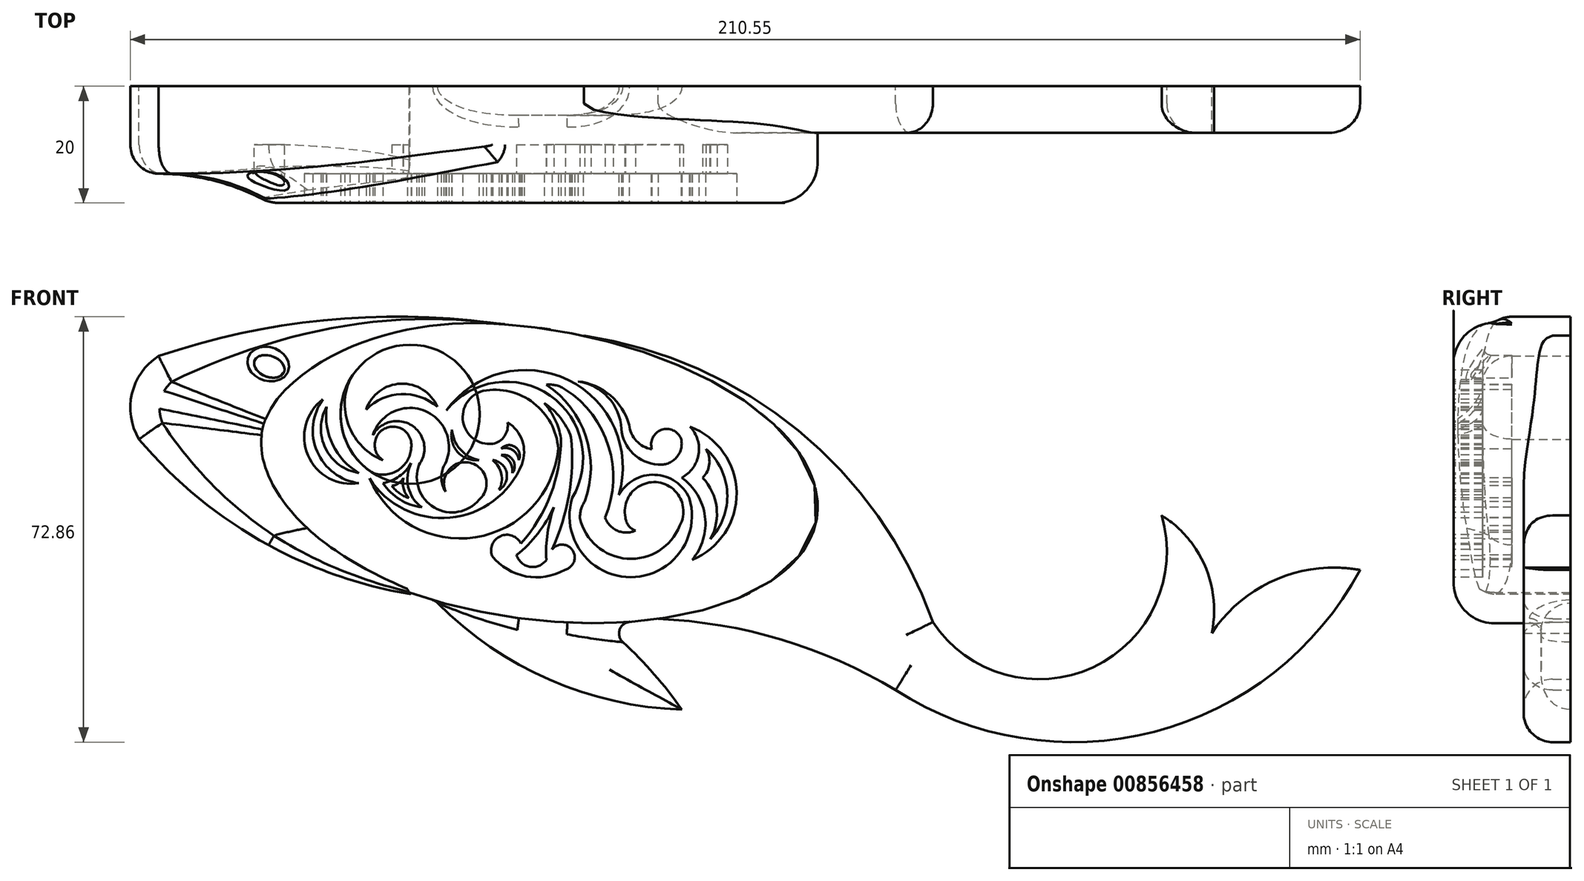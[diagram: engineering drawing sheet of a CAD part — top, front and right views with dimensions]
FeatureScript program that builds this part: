
annotation { "Feature Type Name" : "Feature", "Feature Type Description" : "" }
export const myFeature = defineFeature(function(context is Context, id is Id, definition is map)
    precondition{}
    {
        {
            var Q0;
            Q0=qCreatedBy(makeId("Front.planeOp"),FACE);
            var sketch = newSketch(context, id + "F0", { "sketchPlane" : qUnion([Q0])});
            skEllipse(sketch, "E0", {"center": v(0, 0) * mm, "majorRadius": 50 * mm, "minorRadius": 24.86 * mm, "majorAxis": v(-0.99, 0.15)});
            skArc(sketch, "E1", {"start": v(69.27, -25.55) * mm, "mid": v(46.22, 7.3) * mm, "end": v(9.53, 23.5) * mm});
            skArc(sketch, "E2", {"start": v(62.9, -37.19) * mm, "mid": v(43.33, -28.54) * mm, "end": v(22.22, -25) * mm});
            skArc(sketch, "E3", {"start": v(69.27, -25.55) * mm, "mid": v(96.72, -33.27) * mm, "end": v(108.45, -7.28) * mm});
            skArc(sketch, "E4", {"start": v(62.9, -37.19) * mm, "mid": v(107.17, -44.32) * mm, "end": v(142.42, -16.61) * mm});
            skArc(sketch, "E5", {"start": v(117.03, -27.44) * mm, "mid": v(115.9, -16) * mm, "end": v(108.45, -7.28) * mm});
            skArc(sketch, "E6", {"start": v(142.42, -16.61) * mm, "mid": v(128.1, -18.22) * mm, "end": v(117.03, -27.44) * mm});
            skArc(sketch, "E7", {"start": v(-20.37, -20.5) * mm, "mid": v(-4.53, -37.89) * mm, "end": v(17.35, -46.5) * mm});
            skArc(sketch, "E8", {"start": v(17.35, -46.5) * mm, "mid": v(9.14, -35.42) * mm, "end": v(0, -25.08) * mm});
            skArc(sketch, "E9", {"start": v(-5.05, 25.54) * mm, "mid": v(-34.49, 26.2) * mm, "end": v(-63.28, 20.02) * mm});
            skArc(sketch, "E10", {"start": v(-63.28, 20.02) * mm, "mid": v(-67.85, 13.59) * mm, "end": v(-66.64, 5.79) * mm});
            skArc(sketch, "E11", {"start": v(-66.64, 5.79) * mm, "mid": v(-45.3, -11.9) * mm, "end": v(-19.08, -20.93) * mm});
            skSolve(sketch);
        }
        {
            var Q0;
            {var subQ0=sQuery(id+"F0.wireOp",EDGE,"E0");var subQ5=makeQuery(id+"F0.imprint","INTERSECT",VERTEX,{"derivedFrom":[subQ0,sQuery(id+"F0.wireOp",EDGE,"E7")]});Q0=makeQuery(id+"F0.imprint","IMPRINT",FACE,{"disambiguationData":[TD([[makeQuery(id+"F0.imprint","IMPRINT",EDGE,{"disambiguationData":[TD([[subQ5,-1.0]])],"derivedFrom":subQ0}),1.0]])]});}
            extrude(context, id + "F1", {"entities" : qUnion([Q0]), "depth" : 20 * mm, "offsetDistance" : 25 * mm});
        }
        {
            var Q0;
            {var subQ4=sQuery(id+"F0.wireOp",EDGE,"E9");Q0=makeQuery(id+"F0.imprint","IMPRINT",FACE,{"disambiguationData":[TD([[makeQuery(id+"F0.imprint","IMPRINT",EDGE,{"derivedFrom":subQ4}),1.0]])]});}
            extrude(context, id + "F2", {"entities" : qUnion([Q0]), "operationType" : NewBodyOperationType.ADD, "depth" : 15 * mm, "offsetDistance" : 25 * mm});
        }
        {
            var Q0;
            {var subQ1=sQuery(id+"F0.wireOp",EDGE,"E1");Q0=makeQuery(id+"F0.imprint","IMPRINT",FACE,{"disambiguationData":[TD([[makeQuery(id+"F0.imprint","IMPRINT",EDGE,{"derivedFrom":subQ1}),1.0]])]});}
            extrude(context, id + "F3", {"entities" : qUnion([Q0]), "operationType" : NewBodyOperationType.ADD, "depth" : 8 * mm, "offsetDistance" : 25 * mm});
        }
        {
            var Q0;
            Q0=makeQuery(id+"F1.opExtrude","CAP_EDGE",EDGE,{"disambiguationData":[OSD([sQuery(id+"F0.wireOp",EDGE,"E0")])],"isStart":false});
            fillet(context, id + "F4", {"entities" : qUnion([Q0]), "radius" : 7 * mm, "tangentPropagation" : true, "allowEdgeOverflow" : false});
        }
        {
            var Q0;
            Q0=makeQuery(id+"F2.opExtrude","CAP_EDGE",EDGE,{"disambiguationData":[OSD([sQuery(id+"F0.wireOp",EDGE,"E11")])],"isStart":false});
            var Q1;
            Q1=makeQuery(id+"F2.opExtrude","CAP_EDGE",EDGE,{"disambiguationData":[OSD([sQuery(id+"F0.wireOp",EDGE,"E10")])],"isStart":false});
            var Q2;
            Q2=makeQuery(id+"F2.opExtrude","CAP_EDGE",EDGE,{"disambiguationData":[OSD([sQuery(id+"F0.wireOp",EDGE,"E9")])],"isStart":false});
            fillet(context, id + "F5", {"entities" : qUnion([Q0, Q1, Q2]), "radius" : 5 * mm, "tangentPropagation" : true, "allowEdgeOverflow" : false});
        }
        {
            var Q0;
            Q0=makeQuery(id+"F3.opExtrude","CAP_EDGE",EDGE,{"disambiguationData":[OSD([sQuery(id+"F0.wireOp",EDGE,"E2")])],"isStart":false});
            var Q1;
            Q1=makeQuery(id+"F3.opExtrude","CAP_EDGE",EDGE,{"disambiguationData":[OSD([sQuery(id+"F0.wireOp",EDGE,"E4")])],"isStart":false});
            var Q2;
            Q2=makeQuery(id+"F3.opExtrude","CAP_EDGE",EDGE,{"disambiguationData":[OSD([sQuery(id+"F0.wireOp",EDGE,"E3")])],"isStart":false});
            var Q3;
            Q3=makeQuery(id+"F3.opExtrude","CAP_EDGE",EDGE,{"disambiguationData":[OSD([sQuery(id+"F0.wireOp",EDGE,"E1")])],"isStart":false});
            fillet(context, id + "F6", {"entities" : qUnion([Q0, Q1, Q2, Q3]), "radius" : 5 * mm, "tangentPropagation" : true, "allowEdgeOverflow" : false});
        }
        {
            var Q0;
            {var subQ0=sQuery(id+"F0.wireOp",EDGE,"E0");Q0=makeQuery(id+"F4.opFillet","BLEND_EDGE",EDGE,{"blendedFrom":[makeQuery(id+"F1.opExtrude","CAP_EDGE",EDGE,{"disambiguationData":[OSD([subQ0])],"isStart":false}),makeQuery(id+"F2.opExtrude","CAP_FACE",FACE,{"disambiguationData":[OSD([subQ0,sQuery(id+"F0.wireOp",EDGE,"E7"),sQuery(id+"F0.wireOp",EDGE,"E9"),sQuery(id+"F0.wireOp",EDGE,"E10"),sQuery(id+"F0.wireOp",EDGE,"E11")])],"isStart":false})],"blendedInto":[makeQuery(id+"F2.opExtrude","CAP_FACE",FACE,{"disambiguationData":[OSD([subQ0,sQuery(id+"F0.wireOp",EDGE,"E7"),sQuery(id+"F0.wireOp",EDGE,"E9"),sQuery(id+"F0.wireOp",EDGE,"E10"),sQuery(id+"F0.wireOp",EDGE,"E11")])],"isStart":false})]});}
            var Q1;
            Q1=makeQuery(id+"F3.opExtrude","CAP_EDGE",EDGE,{"disambiguationData":[OSD([sQuery(id+"F0.wireOp",EDGE,"E0")])],"isStart":false});
            fillet(context, id + "F7", {"entities" : qUnion([Q0, Q1]), "radius" : 40 * mm, "tangentPropagation" : true, "allowEdgeOverflow" : false});
        }
        {
            var Q0;
            {var subQ0=sQuery(id+"F0.wireOp",EDGE,"E0");Q0=makeQuery(id+"F3.boolean.opBoolean","MERGE",FACE,{"derivedFrom":[makeQuery(id+"F2.boolean.opBoolean","MERGE",FACE,{"derivedFrom":[makeQuery(id+"F1.opExtrude","CAP_FACE",FACE,{"disambiguationData":[OSD([subQ0])],"isStart":true}),makeQuery(id+"F2.opExtrude","CAP_FACE",FACE,{"disambiguationData":[OSD([subQ0,sQuery(id+"F0.wireOp",EDGE,"E7"),sQuery(id+"F0.wireOp",EDGE,"E9"),sQuery(id+"F0.wireOp",EDGE,"E10"),sQuery(id+"F0.wireOp",EDGE,"E11")])],"isStart":true})]}),makeQuery(id+"F3.opExtrude","CAP_FACE",FACE,{"disambiguationData":[OSD([subQ0,sQuery(id+"F0.wireOp",EDGE,"E1"),sQuery(id+"F0.wireOp",EDGE,"E2"),sQuery(id+"F0.wireOp",EDGE,"E3"),sQuery(id+"F0.wireOp",EDGE,"E4"),sQuery(id+"F0.wireOp",EDGE,"E5"),sQuery(id+"F0.wireOp",EDGE,"E6")])],"isStart":true})]});}
            var sketch = newSketch(context, id + "F8", { "sketchPlane" : qUnion([Q0])});
            skArc(sketch, "E12", {"start": v(-26.32, -40.54) * mm, "mid": v(-3.41, -35.31) * mm, "end": v(15.88, -21.91) * mm});
            skArc(sketch, "E13", {"start": v(-12.39, -25.73) * mm, "mid": v(-19.89, -32.63) * mm, "end": v(-26.32, -40.54) * mm});
            skLineSegment(sketch, "E14", {"start": v(15.88, -21.91) * mm, "end": v(13, -18.53) * mm});
            skLineSegment(sketch, "E15", {"start": v(13, -18.53) * mm, "end": v(-4.62, -20.5) * mm});
            skLineSegment(sketch, "E16", {"start": v(-4.62, -20.5) * mm, "end": v(-12.39, -25.73) * mm});
            skSolve(sketch);
        }
        {
            var Q0;
            Q0 = qSketchRegion(id + "F8", true);
            extrude(context, id + "F9", {"entities" : qUnion([Q0]), "operationType" : NewBodyOperationType.ADD, "oppositeDirection" : true, "depth" : 5 * mm, "offsetDistance" : 25 * mm});
        }
        {
            var Q0;
            Q0=makeQuery(id+"F9.opExtrude","CAP_EDGE",EDGE,{"disambiguationData":[OSD([sQuery(id+"F8.wireOp",EDGE,"E12")])],"isStart":false});
            var Q1;
            Q1=makeQuery(id+"F9.opExtrude","CAP_EDGE",EDGE,{"disambiguationData":[OSD([sQuery(id+"F8.wireOp",EDGE,"E13")])],"isStart":false});
            fillet(context, id + "F10", {"entities" : qUnion([Q0, Q1]), "radius" : 5 * mm, "tangentPropagation" : true, "allowEdgeOverflow" : false});
        }
        {
            var Q0;
            Q0=makeQuery(id+"F9.boolean.opBoolean","INTERSECT",EDGE,{"derivedFrom":[makeQuery(id+"F7.opFillet","SPLIT",FACE,{"disambiguationData":[OD(0.0)],"derivedFrom":makeQuery(id+"F1.opExtrude","SWEPT_FACE",FACE,{"disambiguationData":[OSD([sQuery(id+"F0.wireOp",EDGE,"E0")])]})}),makeQuery(id+"F9.opExtrude","CAP_FACE",FACE,{"disambiguationData":[OSD([sQuery(id+"F8.wireOp",EDGE,"E12"),sQuery(id+"F8.wireOp",EDGE,"E13"),sQuery(id+"F8.wireOp",EDGE,"E14"),sQuery(id+"F8.wireOp",EDGE,"E15"),sQuery(id+"F8.wireOp",EDGE,"E16")])],"isStart":false})]});
            fillet(context, id + "F11", {"entities" : qUnion([Q0]), "radius" : 2 * mm, "tangentPropagation" : true, "allowEdgeOverflow" : false});
        }
        {
            var Q0;
            Q0=makeQuery(id+"F1.opExtrude","CAP_FACE",FACE,{"disambiguationData":[OSD([sQuery(id+"F0.wireOp",EDGE,"E0")])],"isStart":false});
            var sketch = newSketch(context, id + "F12", { "sketchPlane" : qUnion([Q0])});
            skArc(sketch, "E17", {"start": v(-30.55, 15.98) * mm, "mid": v(-31.79, 7.2) * mm, "end": v(-26.62, 0) * mm});
            skArc(sketch, "E18", {"start": v(-26.62, 0) * mm, "mid": v(-22.24, 0.5) * mm, "end": v(-20.04, 4.31) * mm});
            skArc(sketch, "E19", {"start": v(-20.04, 4.31) * mm, "mid": v(-24.4, 7.69) * mm, "end": v(-24.91, 2.2) * mm});
            skArc(sketch, "E20", {"start": v(-30.55, 15.98) * mm, "mid": v(-30.64, 7.9) * mm, "end": v(-24.91, 2.2) * mm});
            skArc(sketch, "E21", {"start": v(-18.7, 1.39) * mm, "mid": v(-19.95, 8.15) * mm, "end": v(-26.62, 6.45) * mm});
            skArc(sketch, "E22", {"start": v(-14.45, 1.16) * mm, "mid": v(-17.59, 10.58) * mm, "end": v(-26.62, 6.45) * mm});
            skArc(sketch, "E23", {"start": v(-18.7, 1.39) * mm, "mid": v(-16.07, -5.94) * mm, "end": v(-8.4, -4.57) * mm});
            skArc(sketch, "E24", {"start": v(-8.4, -4.57) * mm, "mid": v(-9.94, 1.74) * mm, "end": v(-14.16, -3.2) * mm});
            skArc(sketch, "E25", {"start": v(-14.45, 1.16) * mm, "mid": v(-14.87, -1.06) * mm, "end": v(-14.16, -3.2) * mm});
            skArc(sketch, "E26", {"start": v(-13.04, 7.43) * mm, "mid": v(-12.1, 3.6) * mm, "end": v(-8.4, 2.2) * mm});
            skArc(sketch, "E27", {"start": v(-13.04, 7.43) * mm, "mid": v(-11.62, 4.03) * mm, "end": v(-8.4, 2.2) * mm});
            skArc(sketch, "E28", {"start": v(-12.3, 10.8) * mm, "mid": v(-10.81, 4.61) * mm, "end": v(-4.63, 3.08) * mm});
            skArc(sketch, "E29", {"start": v(-12.3, 10.8) * mm, "mid": v(-10.1, 5.32) * mm, "end": v(-4.63, 3.08) * mm});
            skArc(sketch, "E30", {"start": v(-7.7, 14.06) * mm, "mid": v(-11.15, 8.76) * mm, "end": v(-6.08, 5) * mm});
            skArc(sketch, "E31", {"start": v(5.13, 4.18) * mm, "mid": v(0.92, 11.99) * mm, "end": v(-7.7, 14.06) * mm});
            skArc(sketch, "E32", {"start": v(-27.18, -0.93) * mm, "mid": v(-9.02, -11) * mm, "end": v(5.13, 4.18) * mm});
            skArc(sketch, "E33", {"start": v(-6.08, 5) * mm, "mid": v(-4.06, 6.3) * mm, "end": v(-3.52, 8.65) * mm});
            skArc(sketch, "E34", {"start": v(-27.18, -0.93) * mm, "mid": v(-13.39, -7.66) * mm, "end": v(-1.08, 1.5) * mm});
            skArc(sketch, "E35", {"start": v(-1.08, 1.5) * mm, "mid": v(-1.02, 5.52) * mm, "end": v(-3.52, 8.65) * mm});
            skArc(sketch, "E36", {"start": v(-7.07, -4.3) * mm, "mid": v(-6.5, -0.8) * mm, "end": v(-8.4, 2.2) * mm});
            skArc(sketch, "E37", {"start": v(-7.07, -4.3) * mm, "mid": v(-5.57, -0.6) * mm, "end": v(-8.4, 2.2) * mm});
            skArc(sketch, "E38", {"start": v(-4.98, -2.91) * mm, "mid": v(-4.6, -0.15) * mm, "end": v(-6.08, 2.2) * mm});
            skArc(sketch, "E39", {"start": v(-4.98, -2.91) * mm, "mid": v(-3.7, 0.04) * mm, "end": v(-6.08, 2.2) * mm});
            skArc(sketch, "E40", {"start": v(-2.71, 0) * mm, "mid": v(-3.13, 1.88) * mm, "end": v(-4.63, 3.08) * mm});
            skArc(sketch, "E41", {"start": v(-2.71, 0) * mm, "mid": v(-2.61, 2.2) * mm, "end": v(-4.63, 3.08) * mm});
            skArc(sketch, "E42", {"start": v(-1.6, 2.2) * mm, "mid": v(-2.64, 3.92) * mm, "end": v(-4.63, 4.18) * mm});
            skArc(sketch, "E43", {"start": v(-1.6, 2.2) * mm, "mid": v(-2.28, 4.48) * mm, "end": v(-4.63, 4.18) * mm});
            skArc(sketch, "E44", {"start": v(7.52, -4.3) * mm, "mid": v(3.74, 13.27) * mm, "end": v(-14.04, 10.69) * mm});
            skArc(sketch, "E45", {"start": v(15.5, -3.8) * mm, "mid": v(6.85, 15.93) * mm, "end": v(-14.04, 10.69) * mm});
            skArc(sketch, "E46", {"start": v(7.52, -4.3) * mm, "mid": v(17.54, -17.85) * mm, "end": v(27.57, -4.3) * mm});
            skArc(sketch, "E47", {"start": v(27.57, -4.3) * mm, "mid": v(19.95, -0.47) * mm, "end": v(14.67, -7.15) * mm});
            skArc(sketch, "E48", {"start": v(15.94, 7.55) * mm, "mid": v(17.95, 3.33) * mm, "end": v(22.22, 1.45) * mm});
            skArc(sketch, "E49", {"start": v(22.22, 1.45) * mm, "mid": v(25.36, 2.62) * mm, "end": v(26.17, 5.86) * mm});
            skArc(sketch, "E50", {"start": v(26.17, 5.86) * mm, "mid": v(22.8, 7.38) * mm, "end": v(21.17, 4.06) * mm});
            skArc(sketch, "E51", {"start": v(17.28, 8.25) * mm, "mid": v(18.52, 5.5) * mm, "end": v(21.17, 4.06) * mm});
            skArc(sketch, "E52", {"start": v(15.94, 7.55) * mm, "mid": v(13.7, 12.96) * mm, "end": v(8.5, 15.69) * mm});
            skArc(sketch, "E53", {"start": v(17.28, 8.25) * mm, "mid": v(14.03, 13.3) * mm, "end": v(8.5, 15.69) * mm});
            skArc(sketch, "E54", {"start": v(-1.26, -12.1) * mm, "mid": v(-4.72, -10.8) * mm, "end": v(-6.2, -14.19) * mm});
            skArc(sketch, "E55", {"start": v(6.3, -16.57) * mm, "mid": v(7.62, -13.29) * mm, "end": v(4.09, -13.08) * mm});
            skArc(sketch, "E56", {"start": v(-6.2, -14.19) * mm, "mid": v(-0.4, -17.71) * mm, "end": v(6.3, -16.57) * mm});
            skArc(sketch, "E57", {"start": v(-1.26, -12.1) * mm, "mid": v(3.83, -3.72) * mm, "end": v(5.6, 5.92) * mm});
            skArc(sketch, "E58", {"start": v(4.09, -13.08) * mm, "mid": v(6.99, -3.68) * mm, "end": v(7.34, 6.16) * mm});
            skArc(sketch, "E59", {"start": v(5.6, 5.92) * mm, "mid": v(4.6, 9.15) * mm, "end": v(2.75, 11.97) * mm});
            skArc(sketch, "E60", {"start": v(7.34, 6.16) * mm, "mid": v(5.52, 9.43) * mm, "end": v(2.75, 11.97) * mm});
            skArc(sketch, "E61", {"start": v(25.94, -9.01) * mm, "mid": v(22.3, -1.62) * mm, "end": v(16.64, -7.62) * mm});
            skArc(sketch, "E62", {"start": v(8.85, -7.73) * mm, "mid": v(16.92, -14.7) * mm, "end": v(25.94, -9.01) * mm});
            skArc(sketch, "E63", {"start": v(16.64, -7.62) * mm, "mid": v(17.17, -9.02) * mm, "end": v(18.39, -9.88) * mm});
            skArc(sketch, "E64", {"start": v(13.15, -7.62) * mm, "mid": v(15.28, -9.9) * mm, "end": v(18.39, -9.88) * mm});
            skArc(sketch, "E65", {"start": v(13.15, -7.62) * mm, "mid": v(13.75, 4.58) * mm, "end": v(6.35, 14.3) * mm});
            skArc(sketch, "E66", {"start": v(9.67, -4.89) * mm, "mid": v(9.04, -6.25) * mm, "end": v(8.85, -7.73) * mm});
            skArc(sketch, "E67", {"start": v(9.67, -4.89) * mm, "mid": v(9.87, 6.25) * mm, "end": v(3.1, 15.1) * mm});
            skArc(sketch, "E68", {"start": v(6.35, 14.3) * mm, "mid": v(4.8, 15) * mm, "end": v(3.1, 15.1) * mm});
            skArc(sketch, "E69", {"start": v(-15.56, 11.33) * mm, "mid": v(-21.75, 13.5) * mm, "end": v(-27.76, 10.86) * mm});
            skArc(sketch, "E70", {"start": v(-15.56, 11.33) * mm, "mid": v(-21.82, 15.3) * mm, "end": v(-27.76, 10.86) * mm});
            skArc(sketch, "E71", {"start": v(-34.5, 11.33) * mm, "mid": v(-33.47, 4.82) * mm, "end": v(-28.98, 0) * mm});
            skArc(sketch, "E72", {"start": v(-34.5, 11.33) * mm, "mid": v(-34.71, 4.22) * mm, "end": v(-28.98, 0) * mm});
            skArc(sketch, "E73", {"start": v(-35.14, 12.6) * mm, "mid": v(-36.15, 3.67) * mm, "end": v(-28.98, -1.75) * mm});
            skArc(sketch, "E74", {"start": v(-35.14, 12.6) * mm, "mid": v(-37.72, 3) * mm, "end": v(-28.98, -1.75) * mm});
            skArc(sketch, "E75", {"start": v(-24.85, -1.75) * mm, "mid": v(-22.07, -0.56) * mm, "end": v(-20.03, 1.68) * mm});
            skArc(sketch, "E76", {"start": v(-20.03, 1.68) * mm, "mid": v(-20.53, -2.43) * mm, "end": v(-18.23, -5.87) * mm});
            skArc(sketch, "E77", {"start": v(-24.85, -1.75) * mm, "mid": v(-21.99, -4.53) * mm, "end": v(-18.23, -5.87) * mm});
            skArc(sketch, "E78", {"start": v(-23.34, -2.21) * mm, "mid": v(-22.18, -1.76) * mm, "end": v(-21.37, -0.82) * mm});
            skArc(sketch, "E79", {"start": v(-21.37, -0.82) * mm, "mid": v(-21.34, -2.66) * mm, "end": v(-20.45, -4.28) * mm});
            skArc(sketch, "E80", {"start": v(-23.34, -2.21) * mm, "mid": v(-22.06, -3.47) * mm, "end": v(-20.45, -4.28) * mm});
            skArc(sketch, "E81", {"start": v(28.07, -14.9) * mm, "mid": v(30.26, -7.46) * mm, "end": v(26.28, -0.82) * mm});
            skArc(sketch, "E82", {"start": v(26.28, -0.82) * mm, "mid": v(29.17, 3.19) * mm, "end": v(27.71, 7.9) * mm});
            skArc(sketch, "E83", {"start": v(28.07, -14.9) * mm, "mid": v(35.67, -3.37) * mm, "end": v(27.71, 7.9) * mm});
            skArc(sketch, "E84", {"start": v(29.87, -0.82) * mm, "mid": v(31.01, 1.56) * mm, "end": v(30.4, 4.14) * mm});
            skArc(sketch, "E85", {"start": v(31.21, -11.3) * mm, "mid": v(34.07, -3.41) * mm, "end": v(30.4, 4.14) * mm});
            skArc(sketch, "E86", {"start": v(31.21, -11.3) * mm, "mid": v(32.24, -5.84) * mm, "end": v(29.87, -0.82) * mm});
            skArc(sketch, "E87", {"start": v(-2, -14.09) * mm, "mid": v(1.66, -10.35) * mm, "end": v(4.37, -5.87) * mm});
            skArc(sketch, "E88", {"start": v(4.37, -5.87) * mm, "mid": v(3.3, -10.32) * mm, "end": v(3.1, -14.9) * mm});
            skArc(sketch, "E89", {"start": v(-2, -14.09) * mm, "mid": v(0.3, -16.08) * mm, "end": v(3.1, -14.9) * mm});
            skSolve(sketch);
        }
        {
            var Q0;
            Q0=makeQuery(id+"F12.imprint","IMPRINT",FACE,{"disambiguationData":[TD([[makeQuery(id+"F12.imprint","IMPRINT",EDGE,{"derivedFrom":sQuery(id+"F12.wireOp",EDGE,"E17")}),1.0]])]});
            var Q1;
            Q1=makeQuery(id+"F12.imprint","IMPRINT",FACE,{"disambiguationData":[TD([[makeQuery(id+"F12.imprint","IMPRINT",EDGE,{"derivedFrom":sQuery(id+"F12.wireOp",EDGE,"E21")}),-1.0]])]});
            var Q2;
            Q2=makeQuery(id+"F12.imprint","IMPRINT",FACE,{"disambiguationData":[TD([[makeQuery(id+"F12.imprint","IMPRINT",EDGE,{"derivedFrom":sQuery(id+"F12.wireOp",EDGE,"E30")}),1.0]])]});
            var Q3;
            Q3=makeQuery(id+"F12.imprint","IMPRINT",FACE,{"disambiguationData":[TD([[makeQuery(id+"F12.imprint","IMPRINT",EDGE,{"derivedFrom":sQuery(id+"F12.wireOp",EDGE,"E38")}),-1.0]])]});
            var Q4;
            Q4=makeQuery(id+"F12.imprint","IMPRINT",FACE,{"disambiguationData":[TD([[makeQuery(id+"F12.imprint","IMPRINT",EDGE,{"derivedFrom":sQuery(id+"F12.wireOp",EDGE,"E42")}),-1.0]])]});
            var Q5;
            Q5=makeQuery(id+"F12.imprint","IMPRINT",FACE,{"disambiguationData":[TD([[makeQuery(id+"F12.imprint","IMPRINT",EDGE,{"derivedFrom":sQuery(id+"F12.wireOp",EDGE,"E48")}),1.0]])]});
            var Q6;
            Q6=makeQuery(id+"F12.imprint","IMPRINT",FACE,{"disambiguationData":[TD([[makeQuery(id+"F12.imprint","IMPRINT",EDGE,{"derivedFrom":sQuery(id+"F12.wireOp",EDGE,"E69")}),-1.0]])]});
            var Q7;
            Q7=makeQuery(id+"F12.imprint","IMPRINT",FACE,{"disambiguationData":[TD([[makeQuery(id+"F12.imprint","IMPRINT",EDGE,{"derivedFrom":sQuery(id+"F12.wireOp",EDGE,"E71")}),-1.0]])]});
            var Q8;
            Q8=makeQuery(id+"F12.imprint","IMPRINT",FACE,{"disambiguationData":[TD([[makeQuery(id+"F12.imprint","IMPRINT",EDGE,{"derivedFrom":sQuery(id+"F12.wireOp",EDGE,"E44")}),-1.0]])]});
            var Q9;
            Q9=makeQuery(id+"F12.imprint","IMPRINT",FACE,{"disambiguationData":[TD([[makeQuery(id+"F12.imprint","IMPRINT",EDGE,{"derivedFrom":sQuery(id+"F12.wireOp",EDGE,"E54")}),1.0]])]});
            var Q10;
            Q10=makeQuery(id+"F12.imprint","IMPRINT",FACE,{"disambiguationData":[TD([[makeQuery(id+"F12.imprint","IMPRINT",EDGE,{"derivedFrom":sQuery(id+"F12.wireOp",EDGE,"E75")}),-1.0]])]});
            var Q11;
            Q11=makeQuery(id+"F12.imprint","IMPRINT",FACE,{"disambiguationData":[TD([[makeQuery(id+"F12.imprint","IMPRINT",EDGE,{"derivedFrom":sQuery(id+"F12.wireOp",EDGE,"E81")}),-1.0]])]});
            var Q12;
            Q12=makeQuery(id+"F12.imprint","IMPRINT",FACE,{"disambiguationData":[TD([[makeQuery(id+"F12.imprint","IMPRINT",EDGE,{"derivedFrom":sQuery(id+"F12.wireOp",EDGE,"E73")}),-1.0]])]});
            var Q13;
            Q13=makeQuery(id+"F12.imprint","IMPRINT",FACE,{"disambiguationData":[TD([[makeQuery(id+"F12.imprint","IMPRINT",EDGE,{"derivedFrom":sQuery(id+"F12.wireOp",EDGE,"E26")}),1.0]])]});
            var Q14;
            Q14=makeQuery(id+"F12.imprint","IMPRINT",FACE,{"disambiguationData":[TD([[makeQuery(id+"F12.imprint","IMPRINT",EDGE,{"derivedFrom":sQuery(id+"F12.wireOp",EDGE,"E40")}),-1.0]])]});
            extrude(context, id + "F13", {"entities" : qUnion([Q0, Q1, Q2, Q3, Q4, Q5, Q6, Q7, Q8, Q9, Q10, Q11, Q12, Q13, Q14]), "operationType" : NewBodyOperationType.REMOVE, "oppositeDirection" : true, "depth" : 5 * mm, "offsetDistance" : 25 * mm});
        }
        {
            var Q0;
            Q0=makeQuery(id+"F13.boolean.opBoolean","SPLIT",FACE,{"disambiguationData":[TD([makeQuery(id+"F13.opExtrude","SWEPT_FACE",FACE,{"disambiguationData":[OSD([sQuery(id+"F12.wireOp",EDGE,"E87")])]})])],"derivedFrom":makeQuery(id+"F1.opExtrude","CAP_FACE",FACE,{"disambiguationData":[OSD([sQuery(id+"F0.wireOp",EDGE,"E0")])],"isStart":false})});
            var Q1;
            Q1=makeQuery(id+"F13.boolean.opBoolean","SPLIT",FACE,{"disambiguationData":[TD([makeQuery(id+"F13.opExtrude","SWEPT_FACE",FACE,{"disambiguationData":[OSD([sQuery(id+"F12.wireOp",EDGE,"E78")])]})])],"derivedFrom":makeQuery(id+"F1.opExtrude","CAP_FACE",FACE,{"disambiguationData":[OSD([sQuery(id+"F0.wireOp",EDGE,"E0")])],"isStart":false})});
            var Q2;
            Q2=makeQuery(id+"F13.boolean.opBoolean","SPLIT",FACE,{"disambiguationData":[TD([makeQuery(id+"F13.opExtrude","SWEPT_FACE",FACE,{"disambiguationData":[OSD([sQuery(id+"F12.wireOp",EDGE,"E84")])]})])],"derivedFrom":makeQuery(id+"F1.opExtrude","CAP_FACE",FACE,{"disambiguationData":[OSD([sQuery(id+"F0.wireOp",EDGE,"E0")])],"isStart":false})});
            extrude(context, id + "F14", {"entities" : qUnion([Q0, Q1, Q2]), "operationType" : NewBodyOperationType.REMOVE, "oppositeDirection" : true, "depth" : 10 * mm, "offsetDistance" : 25 * mm});
        }
        {
            var Q0;
            {var subQ0=sQuery(id+"F0.wireOp",EDGE,"E0");Q0=makeQuery(id+"F13.boolean.opBoolean","SPLIT",FACE,{"disambiguationData":[TD([makeQuery(id+"F4.opFillet","BLEND_FACE",FACE,{"disambiguationData":[OSD([subQ0])]})])],"derivedFrom":makeQuery(id+"F1.opExtrude","CAP_FACE",FACE,{"disambiguationData":[OSD([subQ0])],"isStart":false})});}
            var sketch = newSketch(context, id + "F15", { "sketchPlane" : qUnion([Q0])});
            skEllipse(sketch, "E90", {"center": v(-44.33, 18.26) * mm, "majorRadius": 2.7 * mm, "minorRadius": 1.8 * mm, "majorAxis": v(0.93, -0.36)});
            skSolve(sketch);
        }
        {
            var Q0;
            Q0 = qSketchRegion(id + "F15", true);
            extrude(context, id + "F16", {"entities" : qUnion([Q0]), "operationType" : NewBodyOperationType.REMOVE, "oppositeDirection" : true, "depth" : 10 * mm, "offsetDistance" : 25 * mm});
        }
        {
            var Q0;
            {var subQ0=sQuery(id+"F0.wireOp",EDGE,"E0");var subQ1=sQuery(id+"F0.wireOp",EDGE,"E9");Q0=makeQuery(id+"F16.boolean.opBoolean","INTERSECT",EDGE,{"derivedFrom":[makeQuery(id+"F7.opFillet","BLEND_FACE",FACE,{"disambiguationData":[OSD([subQ0,subQ1]),TDD([makeQuery(id+"F5.opFillet","BLEND_EDGE",EDGE,{"blendedFrom":[makeQuery(id+"F2.opExtrude","CAP_EDGE",EDGE,{"disambiguationData":[OSD([subQ1])],"isStart":false}),makeQuery(id+"F4.opFillet","BLEND_FACE",FACE,{"disambiguationData":[OSD([subQ0])]})],"blendedInto":[makeQuery(id+"F4.opFillet","BLEND_FACE",FACE,{"disambiguationData":[OSD([subQ0])]})]})])]}),makeQuery(id+"F16.opExtrude","SWEPT_FACE",FACE,{"disambiguationData":[OSD([sQuery(id+"F15.wireOp",EDGE,"E90")])]})]});}
            fillet(context, id + "F17", {"entities" : qUnion([Q0]), "radius" : 1 * mm, "tangentPropagation" : true, "allowEdgeOverflow" : false});
        }
        {
            var Q0;
            Q0=makeQuery(id+"F13.boolean.opBoolean","SPLIT",FACE,{"disambiguationData":[TD([makeQuery(id+"F13.opExtrude","SWEPT_FACE",FACE,{"disambiguationData":[OSD([sQuery(id+"F12.wireOp",EDGE,"E61")])]})])],"derivedFrom":makeQuery(id+"F1.opExtrude","CAP_FACE",FACE,{"disambiguationData":[OSD([sQuery(id+"F0.wireOp",EDGE,"E0")])],"isStart":false})});
            extrude(context, id + "F18", {"entities" : qUnion([Q0]), "operationType" : NewBodyOperationType.REMOVE, "oppositeDirection" : true, "depth" : 10 * mm, "offsetDistance" : 25 * mm});
        }
    });
